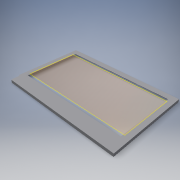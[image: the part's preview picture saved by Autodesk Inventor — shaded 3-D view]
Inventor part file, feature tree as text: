
AUTODESK INVENTOR PART (.ipt)
format: ipt  version: 2017 (Build 210142000, 142)  size: 369,664 bytes
history: native  units: mm
features: extrude x11, sketch x11, projected_geometry x5, other x3, reference x2, plane x1, chamfer x1
ambient origin geometry x8: Origin, YZ Plane, XZ Plane, XY Plane, X Axis, Y Axis, Z Axis, Center Point
bodies: Volumenkörper1 (feature_tree)
feature tree (34):
  plane  "Arbeitsebene1"
  extrude  "Extrusion1"  Depth=1.0mm
  extrude  "Extrusion2"  Depth=1.0mm
  extrude  "Extrusion3"  Depth=1.0mm TaperAngle=0.0deg
  chamfer  "Fase1"  Distance=1.0mm
  extrude  "Extrusion4"  Depth=2.0mm TaperAngle=0.0deg
  extrude  "Extrusion6"  Depth=2.0mm
  extrude  "Extrusion7"  Depth=2.0mm
  extrude  "Extrusion8"  Depth=10.0mm TaperAngle=0.0deg
  extrude  "Extrusion9"  Depth=2.5mm
  extrude  "Extrusion10"  Depth=2.5mm
  extrude  "Extrusion11"  Depth=2.5mm
  extrude  "Extrusion12"  Depth=2.5mm
  sketch  "Skizze1"  dims[d0=1.0mm d1=1.0mm]
  reference  "Referenz1"
  sketch  "Skizze2"  dims[d2=1.0mm d3=1.0mm]
  projected_geometry  "Projizierte Kontur1"
  reference  "Referenz2"
  sketch  "Skizze3"  dims[d4=1.0mm d5=0.0mm d6=1.0mm d7=0.0mm]
  projected_geometry  "Projizierte Kontur2"
  sketch  "Skizze4"  dims[d8=2.0mm]
  projected_geometry  "Projizierte Kontur3"
  sketch  "Skizze9"  dims[d9=2.0mm]
  sketch  "Skizze10"  dims[d10=2.0mm]
  sketch  "Skizze11"  dims[d11=2.0mm d12=1.0mm d13=0.0mm]
  projected_geometry  "Projizierte Kontur8"
  projected_geometry  "Projizierte Kontur9"
  sketch  "Skizze12"  dims[d14=1.0mm d15=2.0mm d16=45.0deg d17=0.7mm d18=0.0mm]
  sketch  "Skizze13"  dims[d21=0.7mm d22=0.0mm d23=2.0mm]
  sketch  "Skizze15"  dims[d24=0.7mm d25=0.0mm d26=2.0mm]
  sketch  "Skizze16"  dims[d27=0.7mm d28=0.0mm d29=0.7mm d30=0.0mm d32=2.5mm d33=2.5mm d34=2.5mm d35=2.5mm d36=1.7mm d37=1.0mm d38=0.0mm d39=0.0mm d40=2.3mm d41=0.0mm d42=10.0mm d43=0.0mm]
  other  "<userpath>\Dropbox\Elektronik\aXe_Dashboard240XL\Gehäuse\DisplayDummyAuschnitt.iam"
  other  "DisplayDummyAuschnitt.iam"
  other  "DisplayDummy:1"
